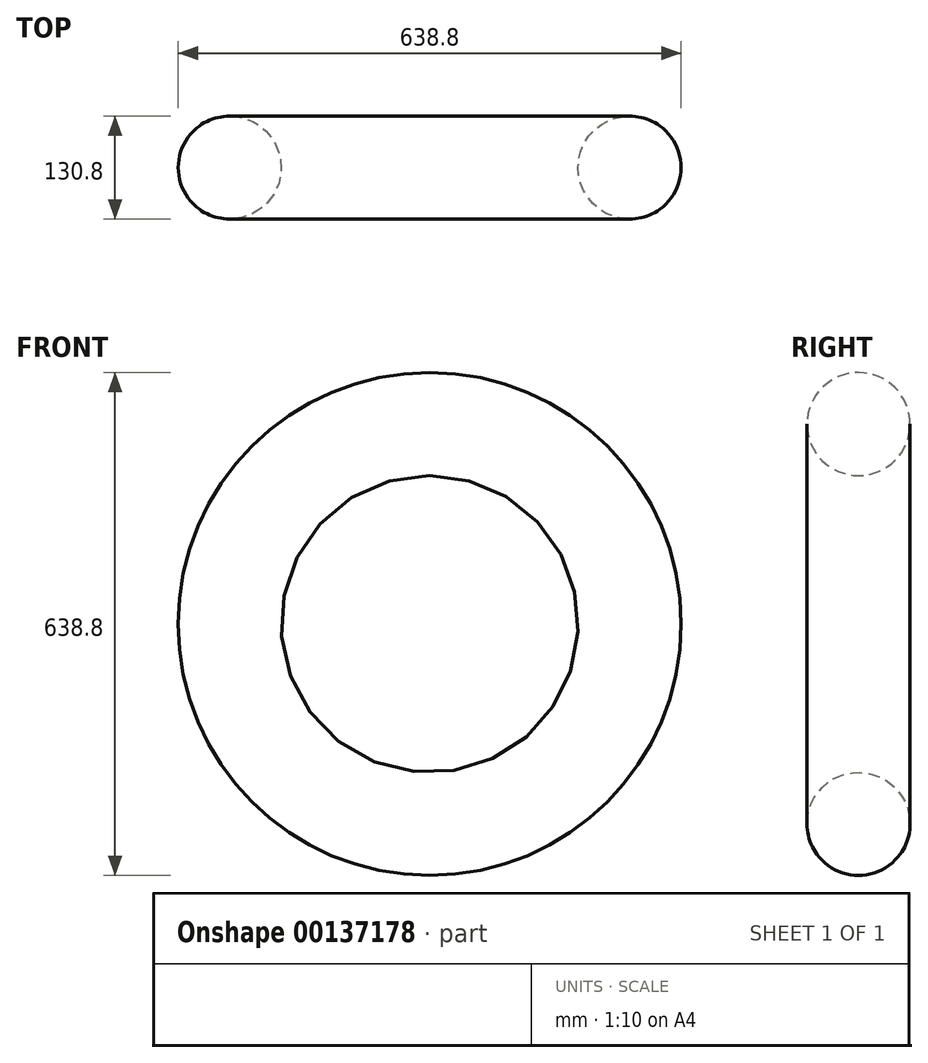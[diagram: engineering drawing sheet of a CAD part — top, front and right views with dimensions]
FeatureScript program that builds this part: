
annotation { "Feature Type Name" : "Feature", "Feature Type Description" : "" }
export const myFeature = defineFeature(function(context is Context, id is Id, definition is map)
    precondition{}
    {
        {
            var Q0;
            Q0=qCreatedBy(makeId("Top.planeOp"),FACE);
            var sketch = newSketch(context, id + "F0", { "sketchPlane" : qUnion([Q0])});
            skCircle(sketch, "E0", {"center": v(0, 0) * mm, "radius": 65.4 * mm});
            skSolve(sketch);
        }
        {
            var Q0;
            Q0=qCreatedBy(makeId("Top.planeOp"),FACE);
            var sketch = newSketch(context, id + "F1", { "sketchPlane" : qUnion([Q0])});
            skLineSegment(sketch, "E1", {"start": v(254, 129) * mm, "end": v(254, -141.43) * mm, "construction": true});
            skSolve(sketch);
        }
        {
            var Q0;
            Q0=makeQuery(id+"F0.imprint","IMPRINT",FACE,{"disambiguationData":[TD([[makeQuery(id+"F0.imprint","IMPRINT",EDGE,{"derivedFrom":sQuery(id+"F0.wireOp",EDGE,"E0")}),1.0]])]});
            var Q1;
            Q1=sQuery(id+"F1.wireOp",EDGE,"E1");
            revolve(context, id + "F2", {"entities" : qUnion([Q0]), "axis" : qUnion([Q1]), "revolveType" : RevolveType.FULL});
        }
    });
